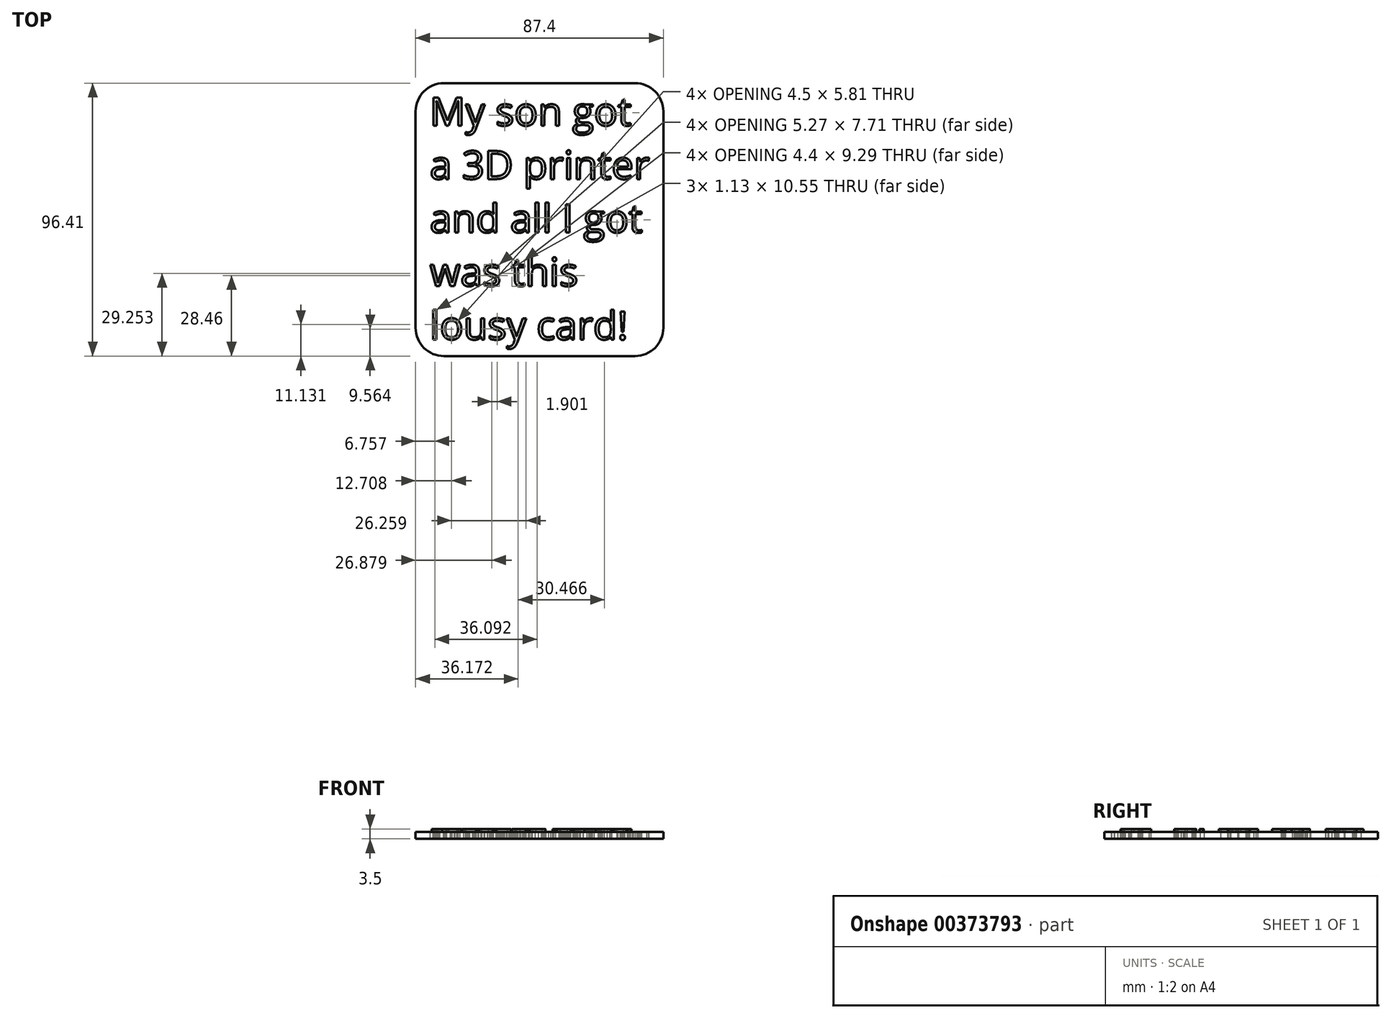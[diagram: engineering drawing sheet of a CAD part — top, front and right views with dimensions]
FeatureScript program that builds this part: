
annotation { "Feature Type Name" : "Feature", "Feature Type Description" : "" }
export const myFeature = defineFeature(function(context is Context, id is Id, definition is map)
    precondition{}
    {
        {
            var Q0;
            Q0=qCreatedBy(makeId("Top.planeOp"),FACE);
            var sketch = newSketch(context, id + "F0", { "sketchPlane" : qUnion([Q0])});
            skText(sketch, "E0", { "text": "My son got  \na 3D printer \nand all I got\nwas this \nlousy card!", "fontName": "OpenSans-Regular.ttf"});
            skLineSegment(sketch, "E1.bottom", {"start": v(0, 0) * mm, "end": v(77.4, 0) * mm, "construction": true});
            skLineSegment(sketch, "E1.top", {"start": v(0, -86.41) * mm, "end": v(77.4, -86.41) * mm, "construction": true});
            skLineSegment(sketch, "E1.left", {"start": v(0, 0) * mm, "end": v(0, -86.41) * mm, "construction": true});
            skLineSegment(sketch, "E1.right", {"start": v(77.4, 0) * mm, "end": v(77.4, -86.41) * mm, "construction": true});
            const initialGuessF0  = {"E0": [0, -0.01, 1, 0, 0.01]};
            skSetInitialGuess(sketch, initialGuessF0);
            skSolve(sketch);
        }
        {
            var Q0;
            Q0=qCreatedBy(makeId("Top.planeOp"),FACE);
            var sketch = newSketch(context, id + "F1", { "sketchPlane" : qUnion([Q0])});
            skLineSegment(sketch, "E2.bottom", {"start": v(-5, 5) * mm, "end": v(82.4, 5) * mm});
            skLineSegment(sketch, "E2.top", {"start": v(-5, -91.41) * mm, "end": v(82.4, -91.41) * mm});
            skLineSegment(sketch, "E2.left", {"start": v(-5, 5) * mm, "end": v(-5, -91.41) * mm});
            skLineSegment(sketch, "E2.right", {"start": v(82.4, 5) * mm, "end": v(82.4, -91.41) * mm});
            skSolve(sketch);
        }
        {
            var Q0;
            Q0=makeQuery(id+"F1.imprint","IMPRINT",FACE,{"disambiguationData":[TD([[makeQuery(id+"F1.imprint","IMPRINT",EDGE,{"derivedFrom":sQuery(id+"F1.wireOp",EDGE,"E2.bottom")}),-1.0]])]});
            extrude(context, id + "F2", {"entities" : qUnion([Q0]), "depth" : 2.5 * mm});
        }
        {
            var Q0;
            Q0 = qSketchRegion(id + "F0", true);
            extrude(context, id + "F3", {"entities" : qUnion([Q0]), "operationType" : NewBodyOperationType.ADD, "depth" : 3.5 * mm});
        }
        {
            var Q0;
            Q0=makeQuery(id+"F3.opExtrude","CAP_FACE",FACE,{"disambiguationData":[OSD([sQuery(id+"F0.wireOp",EDGE,"E0.sketch_text.stroke-18"),sQuery(id+"F0.wireOp",EDGE,"E0.sketch_text.stroke-19"),sQuery(id+"F0.wireOp",EDGE,"E0.sketch_text.stroke-20"),sQuery(id+"F0.wireOp",EDGE,"E0.sketch_text.stroke-21"),sQuery(id+"F0.wireOp",EDGE,"E0.sketch_text.stroke-22"),sQuery(id+"F0.wireOp",EDGE,"E0.sketch_text.stroke-23"),sQuery(id+"F0.wireOp",EDGE,"E0.sketch_text.stroke-24"),sQuery(id+"F0.wireOp",EDGE,"E0.sketch_text.stroke-25"),sQuery(id+"F0.wireOp",EDGE,"E0.sketch_text.stroke-26"),sQuery(id+"F0.wireOp",EDGE,"E0.sketch_text.stroke-27"),sQuery(id+"F0.wireOp",EDGE,"E0.sketch_text.stroke-28"),sQuery(id+"F0.wireOp",EDGE,"E0.sketch_text.stroke-29"),sQuery(id+"F0.wireOp",EDGE,"E0.sketch_text.stroke-30"),sQuery(id+"F0.wireOp",EDGE,"E0.sketch_text.stroke-31"),sQuery(id+"F0.wireOp",EDGE,"E0.sketch_text.stroke-32"),sQuery(id+"F0.wireOp",EDGE,"E0.sketch_text.stroke-33")])],"isStart":false});
            var Q1;
            Q1=makeQuery(id+"F3.opExtrude","CAP_FACE",FACE,{"disambiguationData":[OSD([sQuery(id+"F0.wireOp",EDGE,"E0.sketch_text.stroke-34"),sQuery(id+"F0.wireOp",EDGE,"E0.sketch_text.stroke-35"),sQuery(id+"F0.wireOp",EDGE,"E0.sketch_text.stroke-36"),sQuery(id+"F0.wireOp",EDGE,"E0.sketch_text.stroke-37"),sQuery(id+"F0.wireOp",EDGE,"E0.sketch_text.stroke-38"),sQuery(id+"F0.wireOp",EDGE,"E0.sketch_text.stroke-39"),sQuery(id+"F0.wireOp",EDGE,"E0.sketch_text.stroke-40"),sQuery(id+"F0.wireOp",EDGE,"E0.sketch_text.stroke-41"),sQuery(id+"F0.wireOp",EDGE,"E0.sketch_text.stroke-42"),sQuery(id+"F0.wireOp",EDGE,"E0.sketch_text.stroke-43"),sQuery(id+"F0.wireOp",EDGE,"E0.sketch_text.stroke-44"),sQuery(id+"F0.wireOp",EDGE,"E0.sketch_text.stroke-45"),sQuery(id+"F0.wireOp",EDGE,"E0.sketch_text.stroke-46"),sQuery(id+"F0.wireOp",EDGE,"E0.sketch_text.stroke-47"),sQuery(id+"F0.wireOp",EDGE,"E0.sketch_text.stroke-48"),sQuery(id+"F0.wireOp",EDGE,"E0.sketch_text.stroke-49"),sQuery(id+"F0.wireOp",EDGE,"E0.sketch_text.stroke-50"),sQuery(id+"F0.wireOp",EDGE,"E0.sketch_text.stroke-51"),sQuery(id+"F0.wireOp",EDGE,"E0.sketch_text.stroke-52"),sQuery(id+"F0.wireOp",EDGE,"E0.sketch_text.stroke-53"),sQuery(id+"F0.wireOp",EDGE,"E0.sketch_text.stroke-54"),sQuery(id+"F0.wireOp",EDGE,"E0.sketch_text.stroke-55"),sQuery(id+"F0.wireOp",EDGE,"E0.sketch_text.stroke-56"),sQuery(id+"F0.wireOp",EDGE,"E0.sketch_text.stroke-57"),sQuery(id+"F0.wireOp",EDGE,"E0.sketch_text.stroke-58")])],"isStart":false});
            var Q2;
            Q2=makeQuery(id+"F3.boolean.opBoolean","SPLIT",FACE,{"disambiguationData":[TD([makeQuery(id+"F3.opExtrude","SWEPT_FACE",FACE,{"disambiguationData":[OSD([sQuery(id+"F0.wireOp",EDGE,"E0.sketch_text.stroke-68")])]})])],"derivedFrom":makeQuery(id+"F2.opExtrude","CAP_FACE",FACE,{"disambiguationData":[OSD([sQuery(id+"F1.wireOp",EDGE,"E2.bottom"),sQuery(id+"F1.wireOp",EDGE,"E2.top"),sQuery(id+"F1.wireOp",EDGE,"E2.left"),sQuery(id+"F1.wireOp",EDGE,"E2.right")])],"isStart":false})});
            var Q3;
            Q3=makeQuery(id+"F3.opExtrude","CAP_FACE",FACE,{"disambiguationData":[OSD([sQuery(id+"F0.wireOp",EDGE,"E0.sketch_text.stroke-76"),sQuery(id+"F0.wireOp",EDGE,"E0.sketch_text.stroke-77"),sQuery(id+"F0.wireOp",EDGE,"E0.sketch_text.stroke-78"),sQuery(id+"F0.wireOp",EDGE,"E0.sketch_text.stroke-79"),sQuery(id+"F0.wireOp",EDGE,"E0.sketch_text.stroke-80"),sQuery(id+"F0.wireOp",EDGE,"E0.sketch_text.stroke-81"),sQuery(id+"F0.wireOp",EDGE,"E0.sketch_text.stroke-82"),sQuery(id+"F0.wireOp",EDGE,"E0.sketch_text.stroke-83"),sQuery(id+"F0.wireOp",EDGE,"E0.sketch_text.stroke-84"),sQuery(id+"F0.wireOp",EDGE,"E0.sketch_text.stroke-85"),sQuery(id+"F0.wireOp",EDGE,"E0.sketch_text.stroke-86"),sQuery(id+"F0.wireOp",EDGE,"E0.sketch_text.stroke-87"),sQuery(id+"F0.wireOp",EDGE,"E0.sketch_text.stroke-88"),sQuery(id+"F0.wireOp",EDGE,"E0.sketch_text.stroke-89"),sQuery(id+"F0.wireOp",EDGE,"E0.sketch_text.stroke-90"),sQuery(id+"F0.wireOp",EDGE,"E0.sketch_text.stroke-91"),sQuery(id+"F0.wireOp",EDGE,"E0.sketch_text.stroke-92")])],"isStart":false});
            var Q4;
            Q4=makeQuery(id+"F3.opExtrude","CAP_FACE",FACE,{"disambiguationData":[OSD([sQuery(id+"F0.wireOp",EDGE,"E0.sketch_text.stroke-154"),sQuery(id+"F0.wireOp",EDGE,"E0.sketch_text.stroke-155"),sQuery(id+"F0.wireOp",EDGE,"E0.sketch_text.stroke-156"),sQuery(id+"F0.wireOp",EDGE,"E0.sketch_text.stroke-157"),sQuery(id+"F0.wireOp",EDGE,"E0.sketch_text.stroke-158"),sQuery(id+"F0.wireOp",EDGE,"E0.sketch_text.stroke-159"),sQuery(id+"F0.wireOp",EDGE,"E0.sketch_text.stroke-160"),sQuery(id+"F0.wireOp",EDGE,"E0.sketch_text.stroke-161"),sQuery(id+"F0.wireOp",EDGE,"E0.sketch_text.stroke-162"),sQuery(id+"F0.wireOp",EDGE,"E0.sketch_text.stroke-163"),sQuery(id+"F0.wireOp",EDGE,"E0.sketch_text.stroke-164"),sQuery(id+"F0.wireOp",EDGE,"E0.sketch_text.stroke-165"),sQuery(id+"F0.wireOp",EDGE,"E0.sketch_text.stroke-166"),sQuery(id+"F0.wireOp",EDGE,"E0.sketch_text.stroke-167"),sQuery(id+"F0.wireOp",EDGE,"E0.sketch_text.stroke-168"),sQuery(id+"F0.wireOp",EDGE,"E0.sketch_text.stroke-169"),sQuery(id+"F0.wireOp",EDGE,"E0.sketch_text.stroke-170"),sQuery(id+"F0.wireOp",EDGE,"E0.sketch_text.stroke-171"),sQuery(id+"F0.wireOp",EDGE,"E0.sketch_text.stroke-172")])],"isStart":false});
            var Q5;
            Q5=makeQuery(id+"F3.opExtrude","CAP_FACE",FACE,{"disambiguationData":[OSD([sQuery(id+"F0.wireOp",EDGE,"E0.sketch_text.stroke-200"),sQuery(id+"F0.wireOp",EDGE,"E0.sketch_text.stroke-201"),sQuery(id+"F0.wireOp",EDGE,"E0.sketch_text.stroke-202"),sQuery(id+"F0.wireOp",EDGE,"E0.sketch_text.stroke-203"),sQuery(id+"F0.wireOp",EDGE,"E0.sketch_text.stroke-204"),sQuery(id+"F0.wireOp",EDGE,"E0.sketch_text.stroke-205"),sQuery(id+"F0.wireOp",EDGE,"E0.sketch_text.stroke-206"),sQuery(id+"F0.wireOp",EDGE,"E0.sketch_text.stroke-207"),sQuery(id+"F0.wireOp",EDGE,"E0.sketch_text.stroke-208"),sQuery(id+"F0.wireOp",EDGE,"E0.sketch_text.stroke-209"),sQuery(id+"F0.wireOp",EDGE,"E0.sketch_text.stroke-210"),sQuery(id+"F0.wireOp",EDGE,"E0.sketch_text.stroke-211"),sQuery(id+"F0.wireOp",EDGE,"E0.sketch_text.stroke-212"),sQuery(id+"F0.wireOp",EDGE,"E0.sketch_text.stroke-213"),sQuery(id+"F0.wireOp",EDGE,"E0.sketch_text.stroke-214"),sQuery(id+"F0.wireOp",EDGE,"E0.sketch_text.stroke-215"),sQuery(id+"F0.wireOp",EDGE,"E0.sketch_text.stroke-216"),sQuery(id+"F0.wireOp",EDGE,"E0.sketch_text.stroke-217"),sQuery(id+"F0.wireOp",EDGE,"E0.sketch_text.stroke-218"),sQuery(id+"F0.wireOp",EDGE,"E0.sketch_text.stroke-219"),sQuery(id+"F0.wireOp",EDGE,"E0.sketch_text.stroke-220"),sQuery(id+"F0.wireOp",EDGE,"E0.sketch_text.stroke-221"),sQuery(id+"F0.wireOp",EDGE,"E0.sketch_text.stroke-222"),sQuery(id+"F0.wireOp",EDGE,"E0.sketch_text.stroke-223"),sQuery(id+"F0.wireOp",EDGE,"E0.sketch_text.stroke-224"),sQuery(id+"F0.wireOp",EDGE,"E0.sketch_text.stroke-225"),sQuery(id+"F0.wireOp",EDGE,"E0.sketch_text.stroke-226"),sQuery(id+"F0.wireOp",EDGE,"E0.sketch_text.stroke-227")])],"isStart":false});
            var Q6;
            Q6=makeQuery(id+"F3.opExtrude","CAP_FACE",FACE,{"disambiguationData":[OSD([sQuery(id+"F0.wireOp",EDGE,"E0.sketch_text.stroke-267"),sQuery(id+"F0.wireOp",EDGE,"E0.sketch_text.stroke-268"),sQuery(id+"F0.wireOp",EDGE,"E0.sketch_text.stroke-269"),sQuery(id+"F0.wireOp",EDGE,"E0.sketch_text.stroke-270"),sQuery(id+"F0.wireOp",EDGE,"E0.sketch_text.stroke-271"),sQuery(id+"F0.wireOp",EDGE,"E0.sketch_text.stroke-272"),sQuery(id+"F0.wireOp",EDGE,"E0.sketch_text.stroke-273"),sQuery(id+"F0.wireOp",EDGE,"E0.sketch_text.stroke-274"),sQuery(id+"F0.wireOp",EDGE,"E0.sketch_text.stroke-275"),sQuery(id+"F0.wireOp",EDGE,"E0.sketch_text.stroke-276"),sQuery(id+"F0.wireOp",EDGE,"E0.sketch_text.stroke-277"),sQuery(id+"F0.wireOp",EDGE,"E0.sketch_text.stroke-278"),sQuery(id+"F0.wireOp",EDGE,"E0.sketch_text.stroke-279")])],"isStart":false});
            var Q7;
            Q7=makeQuery(id+"F3.opExtrude","CAP_FACE",FACE,{"disambiguationData":[OSD([sQuery(id+"F0.wireOp",EDGE,"E0.sketch_text.stroke-284"),sQuery(id+"F0.wireOp",EDGE,"E0.sketch_text.stroke-285"),sQuery(id+"F0.wireOp",EDGE,"E0.sketch_text.stroke-286"),sQuery(id+"F0.wireOp",EDGE,"E0.sketch_text.stroke-287"),sQuery(id+"F0.wireOp",EDGE,"E0.sketch_text.stroke-288"),sQuery(id+"F0.wireOp",EDGE,"E0.sketch_text.stroke-289"),sQuery(id+"F0.wireOp",EDGE,"E0.sketch_text.stroke-290"),sQuery(id+"F0.wireOp",EDGE,"E0.sketch_text.stroke-291")])],"isStart":false});
            var Q8;
            Q8=makeQuery(id+"F3.opExtrude","CAP_FACE",FACE,{"disambiguationData":[OSD([sQuery(id+"F0.wireOp",EDGE,"E0.sketch_text.stroke-292"),sQuery(id+"F0.wireOp",EDGE,"E0.sketch_text.stroke-293"),sQuery(id+"F0.wireOp",EDGE,"E0.sketch_text.stroke-294"),sQuery(id+"F0.wireOp",EDGE,"E0.sketch_text.stroke-295"),sQuery(id+"F0.wireOp",EDGE,"E0.sketch_text.stroke-296"),sQuery(id+"F0.wireOp",EDGE,"E0.sketch_text.stroke-297"),sQuery(id+"F0.wireOp",EDGE,"E0.sketch_text.stroke-298"),sQuery(id+"F0.wireOp",EDGE,"E0.sketch_text.stroke-299"),sQuery(id+"F0.wireOp",EDGE,"E0.sketch_text.stroke-300"),sQuery(id+"F0.wireOp",EDGE,"E0.sketch_text.stroke-301"),sQuery(id+"F0.wireOp",EDGE,"E0.sketch_text.stroke-302"),sQuery(id+"F0.wireOp",EDGE,"E0.sketch_text.stroke-303"),sQuery(id+"F0.wireOp",EDGE,"E0.sketch_text.stroke-304"),sQuery(id+"F0.wireOp",EDGE,"E0.sketch_text.stroke-305"),sQuery(id+"F0.wireOp",EDGE,"E0.sketch_text.stroke-306"),sQuery(id+"F0.wireOp",EDGE,"E0.sketch_text.stroke-307"),sQuery(id+"F0.wireOp",EDGE,"E0.sketch_text.stroke-308")])],"isStart":false});
            var Q9;
            Q9=makeQuery(id+"F3.boolean.opBoolean","SPLIT",FACE,{"disambiguationData":[TD([makeQuery(id+"F3.opExtrude","SWEPT_FACE",FACE,{"disambiguationData":[OSD([sQuery(id+"F0.wireOp",EDGE,"E0.sketch_text.stroke-146")])]})])],"derivedFrom":makeQuery(id+"F2.opExtrude","CAP_FACE",FACE,{"disambiguationData":[OSD([sQuery(id+"F1.wireOp",EDGE,"E2.bottom"),sQuery(id+"F1.wireOp",EDGE,"E2.top"),sQuery(id+"F1.wireOp",EDGE,"E2.left"),sQuery(id+"F1.wireOp",EDGE,"E2.right")])],"isStart":false})});
            var Q10;
            Q10=makeQuery(id+"F3.boolean.opBoolean","SPLIT",FACE,{"disambiguationData":[TD([makeQuery(id+"F3.opExtrude","SWEPT_FACE",FACE,{"disambiguationData":[OSD([sQuery(id+"F0.wireOp",EDGE,"E0.sketch_text.stroke-131")])]})])],"derivedFrom":makeQuery(id+"F2.opExtrude","CAP_FACE",FACE,{"disambiguationData":[OSD([sQuery(id+"F1.wireOp",EDGE,"E2.bottom"),sQuery(id+"F1.wireOp",EDGE,"E2.top"),sQuery(id+"F1.wireOp",EDGE,"E2.left"),sQuery(id+"F1.wireOp",EDGE,"E2.right")])],"isStart":false})});
            var Q11;
            Q11=makeQuery(id+"F3.boolean.opBoolean","SPLIT",FACE,{"disambiguationData":[TD([makeQuery(id+"F3.opExtrude","SWEPT_FACE",FACE,{"disambiguationData":[OSD([sQuery(id+"F0.wireOp",EDGE,"E0.sketch_text.stroke-122")])]})])],"derivedFrom":makeQuery(id+"F2.opExtrude","CAP_FACE",FACE,{"disambiguationData":[OSD([sQuery(id+"F1.wireOp",EDGE,"E2.bottom"),sQuery(id+"F1.wireOp",EDGE,"E2.top"),sQuery(id+"F1.wireOp",EDGE,"E2.left"),sQuery(id+"F1.wireOp",EDGE,"E2.right")])],"isStart":false})});
            var Q12;
            Q12=makeQuery(id+"F3.boolean.opBoolean","SPLIT",FACE,{"disambiguationData":[TD([makeQuery(id+"F3.opExtrude","SWEPT_FACE",FACE,{"disambiguationData":[OSD([sQuery(id+"F0.wireOp",EDGE,"E0.sketch_text.stroke-235")])]})])],"derivedFrom":makeQuery(id+"F2.opExtrude","CAP_FACE",FACE,{"disambiguationData":[OSD([sQuery(id+"F1.wireOp",EDGE,"E2.bottom"),sQuery(id+"F1.wireOp",EDGE,"E2.top"),sQuery(id+"F1.wireOp",EDGE,"E2.left"),sQuery(id+"F1.wireOp",EDGE,"E2.right")])],"isStart":false})});
            var Q13;
            Q13=makeQuery(id+"F3.boolean.opBoolean","SPLIT",FACE,{"disambiguationData":[TD([makeQuery(id+"F3.opExtrude","SWEPT_FACE",FACE,{"disambiguationData":[OSD([sQuery(id+"F0.wireOp",EDGE,"E0.sketch_text.stroke-192")])]})])],"derivedFrom":makeQuery(id+"F2.opExtrude","CAP_FACE",FACE,{"disambiguationData":[OSD([sQuery(id+"F1.wireOp",EDGE,"E2.bottom"),sQuery(id+"F1.wireOp",EDGE,"E2.top"),sQuery(id+"F1.wireOp",EDGE,"E2.left"),sQuery(id+"F1.wireOp",EDGE,"E2.right")])],"isStart":false})});
            var Q14;
            Q14=makeQuery(id+"F3.opExtrude","CAP_FACE",FACE,{"disambiguationData":[OSD([sQuery(id+"F0.wireOp",EDGE,"E0.sketch_text.stroke-309"),sQuery(id+"F0.wireOp",EDGE,"E0.sketch_text.stroke-310"),sQuery(id+"F0.wireOp",EDGE,"E0.sketch_text.stroke-311"),sQuery(id+"F0.wireOp",EDGE,"E0.sketch_text.stroke-312"),sQuery(id+"F0.wireOp",EDGE,"E0.sketch_text.stroke-313"),sQuery(id+"F0.wireOp",EDGE,"E0.sketch_text.stroke-314"),sQuery(id+"F0.wireOp",EDGE,"E0.sketch_text.stroke-315"),sQuery(id+"F0.wireOp",EDGE,"E0.sketch_text.stroke-316"),sQuery(id+"F0.wireOp",EDGE,"E0.sketch_text.stroke-317"),sQuery(id+"F0.wireOp",EDGE,"E0.sketch_text.stroke-318"),sQuery(id+"F0.wireOp",EDGE,"E0.sketch_text.stroke-319"),sQuery(id+"F0.wireOp",EDGE,"E0.sketch_text.stroke-320"),sQuery(id+"F0.wireOp",EDGE,"E0.sketch_text.stroke-321"),sQuery(id+"F0.wireOp",EDGE,"E0.sketch_text.stroke-322"),sQuery(id+"F0.wireOp",EDGE,"E0.sketch_text.stroke-323"),sQuery(id+"F0.wireOp",EDGE,"E0.sketch_text.stroke-324"),sQuery(id+"F0.wireOp",EDGE,"E0.sketch_text.stroke-325"),sQuery(id+"F0.wireOp",EDGE,"E0.sketch_text.stroke-326"),sQuery(id+"F0.wireOp",EDGE,"E0.sketch_text.stroke-327")])],"isStart":false});
            var Q15;
            Q15=makeQuery(id+"F3.boolean.opBoolean","SPLIT",FACE,{"disambiguationData":[TD([makeQuery(id+"F3.opExtrude","SWEPT_FACE",FACE,{"disambiguationData":[OSD([sQuery(id+"F0.wireOp",EDGE,"E0.sketch_text.stroke-342")])]})])],"derivedFrom":makeQuery(id+"F2.opExtrude","CAP_FACE",FACE,{"disambiguationData":[OSD([sQuery(id+"F1.wireOp",EDGE,"E2.bottom"),sQuery(id+"F1.wireOp",EDGE,"E2.top"),sQuery(id+"F1.wireOp",EDGE,"E2.left"),sQuery(id+"F1.wireOp",EDGE,"E2.right")])],"isStart":false})});
            var Q16;
            Q16=makeQuery(id+"F3.opExtrude","CAP_FACE",FACE,{"disambiguationData":[OSD([sQuery(id+"F0.wireOp",EDGE,"E0.sketch_text.stroke-347"),sQuery(id+"F0.wireOp",EDGE,"E0.sketch_text.stroke-348"),sQuery(id+"F0.wireOp",EDGE,"E0.sketch_text.stroke-349"),sQuery(id+"F0.wireOp",EDGE,"E0.sketch_text.stroke-350"),sQuery(id+"F0.wireOp",EDGE,"E0.sketch_text.stroke-351"),sQuery(id+"F0.wireOp",EDGE,"E0.sketch_text.stroke-352"),sQuery(id+"F0.wireOp",EDGE,"E0.sketch_text.stroke-353"),sQuery(id+"F0.wireOp",EDGE,"E0.sketch_text.stroke-354"),sQuery(id+"F0.wireOp",EDGE,"E0.sketch_text.stroke-355"),sQuery(id+"F0.wireOp",EDGE,"E0.sketch_text.stroke-356"),sQuery(id+"F0.wireOp",EDGE,"E0.sketch_text.stroke-357"),sQuery(id+"F0.wireOp",EDGE,"E0.sketch_text.stroke-358"),sQuery(id+"F0.wireOp",EDGE,"E0.sketch_text.stroke-359")])],"isStart":false});
            var Q17;
            Q17=makeQuery(id+"F3.boolean.opBoolean","SPLIT",FACE,{"disambiguationData":[TD([makeQuery(id+"F3.opExtrude","SWEPT_FACE",FACE,{"disambiguationData":[OSD([sQuery(id+"F0.wireOp",EDGE,"E0.sketch_text.stroke-379")])]})])],"derivedFrom":makeQuery(id+"F2.opExtrude","CAP_FACE",FACE,{"disambiguationData":[OSD([sQuery(id+"F1.wireOp",EDGE,"E2.bottom"),sQuery(id+"F1.wireOp",EDGE,"E2.top"),sQuery(id+"F1.wireOp",EDGE,"E2.left"),sQuery(id+"F1.wireOp",EDGE,"E2.right")])],"isStart":false})});
            var Q18;
            Q18=makeQuery(id+"F3.opExtrude","CAP_FACE",FACE,{"disambiguationData":[OSD([sQuery(id+"F0.wireOp",EDGE,"E0.sketch_text.stroke-387"),sQuery(id+"F0.wireOp",EDGE,"E0.sketch_text.stroke-388"),sQuery(id+"F0.wireOp",EDGE,"E0.sketch_text.stroke-389"),sQuery(id+"F0.wireOp",EDGE,"E0.sketch_text.stroke-390"),sQuery(id+"F0.wireOp",EDGE,"E0.sketch_text.stroke-391"),sQuery(id+"F0.wireOp",EDGE,"E0.sketch_text.stroke-392"),sQuery(id+"F0.wireOp",EDGE,"E0.sketch_text.stroke-393"),sQuery(id+"F0.wireOp",EDGE,"E0.sketch_text.stroke-394"),sQuery(id+"F0.wireOp",EDGE,"E0.sketch_text.stroke-395"),sQuery(id+"F0.wireOp",EDGE,"E0.sketch_text.stroke-396"),sQuery(id+"F0.wireOp",EDGE,"E0.sketch_text.stroke-397"),sQuery(id+"F0.wireOp",EDGE,"E0.sketch_text.stroke-398"),sQuery(id+"F0.wireOp",EDGE,"E0.sketch_text.stroke-399"),sQuery(id+"F0.wireOp",EDGE,"E0.sketch_text.stroke-400"),sQuery(id+"F0.wireOp",EDGE,"E0.sketch_text.stroke-401"),sQuery(id+"F0.wireOp",EDGE,"E0.sketch_text.stroke-402"),sQuery(id+"F0.wireOp",EDGE,"E0.sketch_text.stroke-403")])],"isStart":false});
            var Q19;
            Q19=makeQuery(id+"F3.boolean.opBoolean","SPLIT",FACE,{"disambiguationData":[TD([makeQuery(id+"F3.opExtrude","SWEPT_FACE",FACE,{"disambiguationData":[OSD([sQuery(id+"F0.wireOp",EDGE,"E0.sketch_text.stroke-419")])]})])],"derivedFrom":makeQuery(id+"F2.opExtrude","CAP_FACE",FACE,{"disambiguationData":[OSD([sQuery(id+"F1.wireOp",EDGE,"E2.bottom"),sQuery(id+"F1.wireOp",EDGE,"E2.top"),sQuery(id+"F1.wireOp",EDGE,"E2.left"),sQuery(id+"F1.wireOp",EDGE,"E2.right")])],"isStart":false})});
            var Q20;
            Q20=makeQuery(id+"F3.boolean.opBoolean","SPLIT",FACE,{"disambiguationData":[TD([makeQuery(id+"F3.opExtrude","SWEPT_FACE",FACE,{"disambiguationData":[OSD([sQuery(id+"F0.wireOp",EDGE,"E0.sketch_text.stroke-447")])]})])],"derivedFrom":makeQuery(id+"F2.opExtrude","CAP_FACE",FACE,{"disambiguationData":[OSD([sQuery(id+"F1.wireOp",EDGE,"E2.bottom"),sQuery(id+"F1.wireOp",EDGE,"E2.top"),sQuery(id+"F1.wireOp",EDGE,"E2.left"),sQuery(id+"F1.wireOp",EDGE,"E2.right")])],"isStart":false})});
            var Q21;
            Q21=makeQuery(id+"F3.opExtrude","CAP_FACE",FACE,{"disambiguationData":[OSD([sQuery(id+"F0.wireOp",EDGE,"E0.sketch_text.stroke-455"),sQuery(id+"F0.wireOp",EDGE,"E0.sketch_text.stroke-456"),sQuery(id+"F0.wireOp",EDGE,"E0.sketch_text.stroke-457"),sQuery(id+"F0.wireOp",EDGE,"E0.sketch_text.stroke-458")])],"isStart":false});
            var Q22;
            Q22=makeQuery(id+"F3.opExtrude","CAP_FACE",FACE,{"disambiguationData":[OSD([sQuery(id+"F0.wireOp",EDGE,"E0.sketch_text.stroke-459"),sQuery(id+"F0.wireOp",EDGE,"E0.sketch_text.stroke-460"),sQuery(id+"F0.wireOp",EDGE,"E0.sketch_text.stroke-461"),sQuery(id+"F0.wireOp",EDGE,"E0.sketch_text.stroke-462")])],"isStart":false});
            var Q23;
            Q23=makeQuery(id+"F3.opExtrude","CAP_FACE",FACE,{"disambiguationData":[OSD([sQuery(id+"F0.wireOp",EDGE,"E0.sketch_text.stroke-463"),sQuery(id+"F0.wireOp",EDGE,"E0.sketch_text.stroke-464"),sQuery(id+"F0.wireOp",EDGE,"E0.sketch_text.stroke-465"),sQuery(id+"F0.wireOp",EDGE,"E0.sketch_text.stroke-466")])],"isStart":false});
            var Q24;
            Q24=makeQuery(id+"F3.boolean.opBoolean","SPLIT",FACE,{"disambiguationData":[TD([makeQuery(id+"F3.opExtrude","SWEPT_FACE",FACE,{"disambiguationData":[OSD([sQuery(id+"F0.wireOp",EDGE,"E0.sketch_text.stroke-505")])]})])],"derivedFrom":makeQuery(id+"F2.opExtrude","CAP_FACE",FACE,{"disambiguationData":[OSD([sQuery(id+"F1.wireOp",EDGE,"E2.bottom"),sQuery(id+"F1.wireOp",EDGE,"E2.top"),sQuery(id+"F1.wireOp",EDGE,"E2.left"),sQuery(id+"F1.wireOp",EDGE,"E2.right")])],"isStart":false})});
            var Q25;
            Q25=makeQuery(id+"F3.boolean.opBoolean","SPLIT",FACE,{"disambiguationData":[TD([makeQuery(id+"F3.opExtrude","SWEPT_FACE",FACE,{"disambiguationData":[OSD([sQuery(id+"F0.wireOp",EDGE,"E0.sketch_text.stroke-496")])]})])],"derivedFrom":makeQuery(id+"F2.opExtrude","CAP_FACE",FACE,{"disambiguationData":[OSD([sQuery(id+"F1.wireOp",EDGE,"E2.bottom"),sQuery(id+"F1.wireOp",EDGE,"E2.top"),sQuery(id+"F1.wireOp",EDGE,"E2.left"),sQuery(id+"F1.wireOp",EDGE,"E2.right")])],"isStart":false})});
            var Q26;
            Q26=makeQuery(id+"F3.boolean.opBoolean","SPLIT",FACE,{"disambiguationData":[TD([makeQuery(id+"F3.opExtrude","SWEPT_FACE",FACE,{"disambiguationData":[OSD([sQuery(id+"F0.wireOp",EDGE,"E0.sketch_text.stroke-520")])]})])],"derivedFrom":makeQuery(id+"F2.opExtrude","CAP_FACE",FACE,{"disambiguationData":[OSD([sQuery(id+"F1.wireOp",EDGE,"E2.bottom"),sQuery(id+"F1.wireOp",EDGE,"E2.top"),sQuery(id+"F1.wireOp",EDGE,"E2.left"),sQuery(id+"F1.wireOp",EDGE,"E2.right")])],"isStart":false})});
            var Q27;
            Q27=makeQuery(id+"F3.opExtrude","CAP_FACE",FACE,{"disambiguationData":[OSD([sQuery(id+"F0.wireOp",EDGE,"E0.sketch_text.stroke-528"),sQuery(id+"F0.wireOp",EDGE,"E0.sketch_text.stroke-529"),sQuery(id+"F0.wireOp",EDGE,"E0.sketch_text.stroke-530"),sQuery(id+"F0.wireOp",EDGE,"E0.sketch_text.stroke-531"),sQuery(id+"F0.wireOp",EDGE,"E0.sketch_text.stroke-532"),sQuery(id+"F0.wireOp",EDGE,"E0.sketch_text.stroke-533"),sQuery(id+"F0.wireOp",EDGE,"E0.sketch_text.stroke-534"),sQuery(id+"F0.wireOp",EDGE,"E0.sketch_text.stroke-535"),sQuery(id+"F0.wireOp",EDGE,"E0.sketch_text.stroke-536"),sQuery(id+"F0.wireOp",EDGE,"E0.sketch_text.stroke-537"),sQuery(id+"F0.wireOp",EDGE,"E0.sketch_text.stroke-538"),sQuery(id+"F0.wireOp",EDGE,"E0.sketch_text.stroke-539"),sQuery(id+"F0.wireOp",EDGE,"E0.sketch_text.stroke-540"),sQuery(id+"F0.wireOp",EDGE,"E0.sketch_text.stroke-541"),sQuery(id+"F0.wireOp",EDGE,"E0.sketch_text.stroke-542"),sQuery(id+"F0.wireOp",EDGE,"E0.sketch_text.stroke-543"),sQuery(id+"F0.wireOp",EDGE,"E0.sketch_text.stroke-544"),sQuery(id+"F0.wireOp",EDGE,"E0.sketch_text.stroke-545"),sQuery(id+"F0.wireOp",EDGE,"E0.sketch_text.stroke-546")])],"isStart":false});
            var Q28;
            Q28=makeQuery(id+"F3.opExtrude","CAP_FACE",FACE,{"disambiguationData":[OSD([sQuery(id+"F0.wireOp",EDGE,"E0.sketch_text.stroke-547"),sQuery(id+"F0.wireOp",EDGE,"E0.sketch_text.stroke-548"),sQuery(id+"F0.wireOp",EDGE,"E0.sketch_text.stroke-549"),sQuery(id+"F0.wireOp",EDGE,"E0.sketch_text.stroke-550"),sQuery(id+"F0.wireOp",EDGE,"E0.sketch_text.stroke-551"),sQuery(id+"F0.wireOp",EDGE,"E0.sketch_text.stroke-552"),sQuery(id+"F0.wireOp",EDGE,"E0.sketch_text.stroke-553"),sQuery(id+"F0.wireOp",EDGE,"E0.sketch_text.stroke-554"),sQuery(id+"F0.wireOp",EDGE,"E0.sketch_text.stroke-555"),sQuery(id+"F0.wireOp",EDGE,"E0.sketch_text.stroke-556"),sQuery(id+"F0.wireOp",EDGE,"E0.sketch_text.stroke-557"),sQuery(id+"F0.wireOp",EDGE,"E0.sketch_text.stroke-558"),sQuery(id+"F0.wireOp",EDGE,"E0.sketch_text.stroke-559"),sQuery(id+"F0.wireOp",EDGE,"E0.sketch_text.stroke-560"),sQuery(id+"F0.wireOp",EDGE,"E0.sketch_text.stroke-561"),sQuery(id+"F0.wireOp",EDGE,"E0.sketch_text.stroke-562"),sQuery(id+"F0.wireOp",EDGE,"E0.sketch_text.stroke-563"),sQuery(id+"F0.wireOp",EDGE,"E0.sketch_text.stroke-564"),sQuery(id+"F0.wireOp",EDGE,"E0.sketch_text.stroke-565"),sQuery(id+"F0.wireOp",EDGE,"E0.sketch_text.stroke-566"),sQuery(id+"F0.wireOp",EDGE,"E0.sketch_text.stroke-567"),sQuery(id+"F0.wireOp",EDGE,"E0.sketch_text.stroke-568"),sQuery(id+"F0.wireOp",EDGE,"E0.sketch_text.stroke-569")])],"isStart":false});
            var Q29;
            Q29=makeQuery(id+"F3.boolean.opBoolean","SPLIT",FACE,{"disambiguationData":[TD([makeQuery(id+"F3.opExtrude","SWEPT_FACE",FACE,{"disambiguationData":[OSD([sQuery(id+"F0.wireOp",EDGE,"E0.sketch_text.stroke-589")])]})])],"derivedFrom":makeQuery(id+"F2.opExtrude","CAP_FACE",FACE,{"disambiguationData":[OSD([sQuery(id+"F1.wireOp",EDGE,"E2.bottom"),sQuery(id+"F1.wireOp",EDGE,"E2.top"),sQuery(id+"F1.wireOp",EDGE,"E2.left"),sQuery(id+"F1.wireOp",EDGE,"E2.right")])],"isStart":false})});
            var Q30;
            Q30=makeQuery(id+"F3.opExtrude","CAP_FACE",FACE,{"disambiguationData":[OSD([sQuery(id+"F0.wireOp",EDGE,"E0.sketch_text.stroke-597"),sQuery(id+"F0.wireOp",EDGE,"E0.sketch_text.stroke-598"),sQuery(id+"F0.wireOp",EDGE,"E0.sketch_text.stroke-599"),sQuery(id+"F0.wireOp",EDGE,"E0.sketch_text.stroke-600"),sQuery(id+"F0.wireOp",EDGE,"E0.sketch_text.stroke-601"),sQuery(id+"F0.wireOp",EDGE,"E0.sketch_text.stroke-602"),sQuery(id+"F0.wireOp",EDGE,"E0.sketch_text.stroke-603"),sQuery(id+"F0.wireOp",EDGE,"E0.sketch_text.stroke-604"),sQuery(id+"F0.wireOp",EDGE,"E0.sketch_text.stroke-605"),sQuery(id+"F0.wireOp",EDGE,"E0.sketch_text.stroke-606"),sQuery(id+"F0.wireOp",EDGE,"E0.sketch_text.stroke-607"),sQuery(id+"F0.wireOp",EDGE,"E0.sketch_text.stroke-608"),sQuery(id+"F0.wireOp",EDGE,"E0.sketch_text.stroke-609"),sQuery(id+"F0.wireOp",EDGE,"E0.sketch_text.stroke-610"),sQuery(id+"F0.wireOp",EDGE,"E0.sketch_text.stroke-611"),sQuery(id+"F0.wireOp",EDGE,"E0.sketch_text.stroke-612"),sQuery(id+"F0.wireOp",EDGE,"E0.sketch_text.stroke-613"),sQuery(id+"F0.wireOp",EDGE,"E0.sketch_text.stroke-614"),sQuery(id+"F0.wireOp",EDGE,"E0.sketch_text.stroke-615"),sQuery(id+"F0.wireOp",EDGE,"E0.sketch_text.stroke-616"),sQuery(id+"F0.wireOp",EDGE,"E0.sketch_text.stroke-617"),sQuery(id+"F0.wireOp",EDGE,"E0.sketch_text.stroke-618"),sQuery(id+"F0.wireOp",EDGE,"E0.sketch_text.stroke-619"),sQuery(id+"F0.wireOp",EDGE,"E0.sketch_text.stroke-620"),sQuery(id+"F0.wireOp",EDGE,"E0.sketch_text.stroke-621")])],"isStart":false});
            var Q31;
            Q31=makeQuery(id+"F3.opExtrude","CAP_FACE",FACE,{"disambiguationData":[OSD([sQuery(id+"F0.wireOp",EDGE,"E0.sketch_text.stroke-622"),sQuery(id+"F0.wireOp",EDGE,"E0.sketch_text.stroke-623"),sQuery(id+"F0.wireOp",EDGE,"E0.sketch_text.stroke-624"),sQuery(id+"F0.wireOp",EDGE,"E0.sketch_text.stroke-625"),sQuery(id+"F0.wireOp",EDGE,"E0.sketch_text.stroke-626"),sQuery(id+"F0.wireOp",EDGE,"E0.sketch_text.stroke-627"),sQuery(id+"F0.wireOp",EDGE,"E0.sketch_text.stroke-628"),sQuery(id+"F0.wireOp",EDGE,"E0.sketch_text.stroke-629"),sQuery(id+"F0.wireOp",EDGE,"E0.sketch_text.stroke-630"),sQuery(id+"F0.wireOp",EDGE,"E0.sketch_text.stroke-631"),sQuery(id+"F0.wireOp",EDGE,"E0.sketch_text.stroke-632"),sQuery(id+"F0.wireOp",EDGE,"E0.sketch_text.stroke-633"),sQuery(id+"F0.wireOp",EDGE,"E0.sketch_text.stroke-634"),sQuery(id+"F0.wireOp",EDGE,"E0.sketch_text.stroke-635"),sQuery(id+"F0.wireOp",EDGE,"E0.sketch_text.stroke-636"),sQuery(id+"F0.wireOp",EDGE,"E0.sketch_text.stroke-637"),sQuery(id+"F0.wireOp",EDGE,"E0.sketch_text.stroke-638"),sQuery(id+"F0.wireOp",EDGE,"E0.sketch_text.stroke-639"),sQuery(id+"F0.wireOp",EDGE,"E0.sketch_text.stroke-640")])],"isStart":false});
            var Q32;
            Q32=makeQuery(id+"F3.opExtrude","CAP_FACE",FACE,{"disambiguationData":[OSD([sQuery(id+"F0.wireOp",EDGE,"E0.sketch_text.stroke-641"),sQuery(id+"F0.wireOp",EDGE,"E0.sketch_text.stroke-642"),sQuery(id+"F0.wireOp",EDGE,"E0.sketch_text.stroke-643"),sQuery(id+"F0.wireOp",EDGE,"E0.sketch_text.stroke-644"),sQuery(id+"F0.wireOp",EDGE,"E0.sketch_text.stroke-645"),sQuery(id+"F0.wireOp",EDGE,"E0.sketch_text.stroke-646"),sQuery(id+"F0.wireOp",EDGE,"E0.sketch_text.stroke-647"),sQuery(id+"F0.wireOp",EDGE,"E0.sketch_text.stroke-648"),sQuery(id+"F0.wireOp",EDGE,"E0.sketch_text.stroke-649"),sQuery(id+"F0.wireOp",EDGE,"E0.sketch_text.stroke-650"),sQuery(id+"F0.wireOp",EDGE,"E0.sketch_text.stroke-651"),sQuery(id+"F0.wireOp",EDGE,"E0.sketch_text.stroke-652"),sQuery(id+"F0.wireOp",EDGE,"E0.sketch_text.stroke-653"),sQuery(id+"F0.wireOp",EDGE,"E0.sketch_text.stroke-654"),sQuery(id+"F0.wireOp",EDGE,"E0.sketch_text.stroke-655"),sQuery(id+"F0.wireOp",EDGE,"E0.sketch_text.stroke-656"),sQuery(id+"F0.wireOp",EDGE,"E0.sketch_text.stroke-657"),sQuery(id+"F0.wireOp",EDGE,"E0.sketch_text.stroke-658")])],"isStart":false});
            var Q33;
            Q33=makeQuery(id+"F3.opExtrude","CAP_FACE",FACE,{"disambiguationData":[OSD([sQuery(id+"F0.wireOp",EDGE,"E0.sketch_text.stroke-659"),sQuery(id+"F0.wireOp",EDGE,"E0.sketch_text.stroke-660"),sQuery(id+"F0.wireOp",EDGE,"E0.sketch_text.stroke-661"),sQuery(id+"F0.wireOp",EDGE,"E0.sketch_text.stroke-662")])],"isStart":false});
            var Q34;
            Q34=makeQuery(id+"F3.opExtrude","CAP_FACE",FACE,{"disambiguationData":[OSD([sQuery(id+"F0.wireOp",EDGE,"E0.sketch_text.stroke-671"),sQuery(id+"F0.wireOp",EDGE,"E0.sketch_text.stroke-672"),sQuery(id+"F0.wireOp",EDGE,"E0.sketch_text.stroke-673"),sQuery(id+"F0.wireOp",EDGE,"E0.sketch_text.stroke-674"),sQuery(id+"F0.wireOp",EDGE,"E0.sketch_text.stroke-675"),sQuery(id+"F0.wireOp",EDGE,"E0.sketch_text.stroke-676"),sQuery(id+"F0.wireOp",EDGE,"E0.sketch_text.stroke-677"),sQuery(id+"F0.wireOp",EDGE,"E0.sketch_text.stroke-678"),sQuery(id+"F0.wireOp",EDGE,"E0.sketch_text.stroke-679"),sQuery(id+"F0.wireOp",EDGE,"E0.sketch_text.stroke-680"),sQuery(id+"F0.wireOp",EDGE,"E0.sketch_text.stroke-681"),sQuery(id+"F0.wireOp",EDGE,"E0.sketch_text.stroke-682"),sQuery(id+"F0.wireOp",EDGE,"E0.sketch_text.stroke-683"),sQuery(id+"F0.wireOp",EDGE,"E0.sketch_text.stroke-684"),sQuery(id+"F0.wireOp",EDGE,"E0.sketch_text.stroke-685"),sQuery(id+"F0.wireOp",EDGE,"E0.sketch_text.stroke-686"),sQuery(id+"F0.wireOp",EDGE,"E0.sketch_text.stroke-687"),sQuery(id+"F0.wireOp",EDGE,"E0.sketch_text.stroke-688"),sQuery(id+"F0.wireOp",EDGE,"E0.sketch_text.stroke-689"),sQuery(id+"F0.wireOp",EDGE,"E0.sketch_text.stroke-690"),sQuery(id+"F0.wireOp",EDGE,"E0.sketch_text.stroke-691"),sQuery(id+"F0.wireOp",EDGE,"E0.sketch_text.stroke-692"),sQuery(id+"F0.wireOp",EDGE,"E0.sketch_text.stroke-693"),sQuery(id+"F0.wireOp",EDGE,"E0.sketch_text.stroke-694"),sQuery(id+"F0.wireOp",EDGE,"E0.sketch_text.stroke-695")])],"isStart":false});
            var Q35;
            Q35=makeQuery(id+"F3.opExtrude","CAP_FACE",FACE,{"disambiguationData":[OSD([sQuery(id+"F0.wireOp",EDGE,"E0.sketch_text.stroke-696"),sQuery(id+"F0.wireOp",EDGE,"E0.sketch_text.stroke-697"),sQuery(id+"F0.wireOp",EDGE,"E0.sketch_text.stroke-698"),sQuery(id+"F0.wireOp",EDGE,"E0.sketch_text.stroke-699")])],"isStart":false});
            var Q36;
            Q36=makeQuery(id+"F3.boolean.opBoolean","SPLIT",FACE,{"disambiguationData":[TD([makeQuery(id+"F3.opExtrude","SWEPT_FACE",FACE,{"disambiguationData":[OSD([sQuery(id+"F0.wireOp",EDGE,"E0.sketch_text.stroke-709")])]})])],"derivedFrom":makeQuery(id+"F2.opExtrude","CAP_FACE",FACE,{"disambiguationData":[OSD([sQuery(id+"F1.wireOp",EDGE,"E2.bottom"),sQuery(id+"F1.wireOp",EDGE,"E2.top"),sQuery(id+"F1.wireOp",EDGE,"E2.left"),sQuery(id+"F1.wireOp",EDGE,"E2.right")])],"isStart":false})});
            var Q37;
            Q37=makeQuery(id+"F3.opExtrude","CAP_FACE",FACE,{"disambiguationData":[OSD([sQuery(id+"F0.wireOp",EDGE,"E0.sketch_text.stroke-717"),sQuery(id+"F0.wireOp",EDGE,"E0.sketch_text.stroke-718"),sQuery(id+"F0.wireOp",EDGE,"E0.sketch_text.stroke-719"),sQuery(id+"F0.wireOp",EDGE,"E0.sketch_text.stroke-720"),sQuery(id+"F0.wireOp",EDGE,"E0.sketch_text.stroke-721"),sQuery(id+"F0.wireOp",EDGE,"E0.sketch_text.stroke-722"),sQuery(id+"F0.wireOp",EDGE,"E0.sketch_text.stroke-723"),sQuery(id+"F0.wireOp",EDGE,"E0.sketch_text.stroke-724"),sQuery(id+"F0.wireOp",EDGE,"E0.sketch_text.stroke-725"),sQuery(id+"F0.wireOp",EDGE,"E0.sketch_text.stroke-726"),sQuery(id+"F0.wireOp",EDGE,"E0.sketch_text.stroke-727"),sQuery(id+"F0.wireOp",EDGE,"E0.sketch_text.stroke-728"),sQuery(id+"F0.wireOp",EDGE,"E0.sketch_text.stroke-729"),sQuery(id+"F0.wireOp",EDGE,"E0.sketch_text.stroke-730"),sQuery(id+"F0.wireOp",EDGE,"E0.sketch_text.stroke-731"),sQuery(id+"F0.wireOp",EDGE,"E0.sketch_text.stroke-732"),sQuery(id+"F0.wireOp",EDGE,"E0.sketch_text.stroke-733")])],"isStart":false});
            var Q38;
            Q38=makeQuery(id+"F3.opExtrude","CAP_FACE",FACE,{"disambiguationData":[OSD([sQuery(id+"F0.wireOp",EDGE,"E0.sketch_text.stroke-734"),sQuery(id+"F0.wireOp",EDGE,"E0.sketch_text.stroke-735"),sQuery(id+"F0.wireOp",EDGE,"E0.sketch_text.stroke-736"),sQuery(id+"F0.wireOp",EDGE,"E0.sketch_text.stroke-737"),sQuery(id+"F0.wireOp",EDGE,"E0.sketch_text.stroke-738"),sQuery(id+"F0.wireOp",EDGE,"E0.sketch_text.stroke-739"),sQuery(id+"F0.wireOp",EDGE,"E0.sketch_text.stroke-740"),sQuery(id+"F0.wireOp",EDGE,"E0.sketch_text.stroke-741"),sQuery(id+"F0.wireOp",EDGE,"E0.sketch_text.stroke-742"),sQuery(id+"F0.wireOp",EDGE,"E0.sketch_text.stroke-743"),sQuery(id+"F0.wireOp",EDGE,"E0.sketch_text.stroke-744"),sQuery(id+"F0.wireOp",EDGE,"E0.sketch_text.stroke-745"),sQuery(id+"F0.wireOp",EDGE,"E0.sketch_text.stroke-746"),sQuery(id+"F0.wireOp",EDGE,"E0.sketch_text.stroke-747"),sQuery(id+"F0.wireOp",EDGE,"E0.sketch_text.stroke-748"),sQuery(id+"F0.wireOp",EDGE,"E0.sketch_text.stroke-749"),sQuery(id+"F0.wireOp",EDGE,"E0.sketch_text.stroke-750"),sQuery(id+"F0.wireOp",EDGE,"E0.sketch_text.stroke-751"),sQuery(id+"F0.wireOp",EDGE,"E0.sketch_text.stroke-752"),sQuery(id+"F0.wireOp",EDGE,"E0.sketch_text.stroke-753"),sQuery(id+"F0.wireOp",EDGE,"E0.sketch_text.stroke-754"),sQuery(id+"F0.wireOp",EDGE,"E0.sketch_text.stroke-755"),sQuery(id+"F0.wireOp",EDGE,"E0.sketch_text.stroke-756"),sQuery(id+"F0.wireOp",EDGE,"E0.sketch_text.stroke-757"),sQuery(id+"F0.wireOp",EDGE,"E0.sketch_text.stroke-758")])],"isStart":false});
            var Q39;
            Q39=makeQuery(id+"F3.opExtrude","CAP_FACE",FACE,{"disambiguationData":[OSD([sQuery(id+"F0.wireOp",EDGE,"E0.sketch_text.stroke-759"),sQuery(id+"F0.wireOp",EDGE,"E0.sketch_text.stroke-760"),sQuery(id+"F0.wireOp",EDGE,"E0.sketch_text.stroke-761"),sQuery(id+"F0.wireOp",EDGE,"E0.sketch_text.stroke-762"),sQuery(id+"F0.wireOp",EDGE,"E0.sketch_text.stroke-763"),sQuery(id+"F0.wireOp",EDGE,"E0.sketch_text.stroke-764"),sQuery(id+"F0.wireOp",EDGE,"E0.sketch_text.stroke-765"),sQuery(id+"F0.wireOp",EDGE,"E0.sketch_text.stroke-766"),sQuery(id+"F0.wireOp",EDGE,"E0.sketch_text.stroke-767"),sQuery(id+"F0.wireOp",EDGE,"E0.sketch_text.stroke-768"),sQuery(id+"F0.wireOp",EDGE,"E0.sketch_text.stroke-769"),sQuery(id+"F0.wireOp",EDGE,"E0.sketch_text.stroke-770"),sQuery(id+"F0.wireOp",EDGE,"E0.sketch_text.stroke-771"),sQuery(id+"F0.wireOp",EDGE,"E0.sketch_text.stroke-772"),sQuery(id+"F0.wireOp",EDGE,"E0.sketch_text.stroke-773"),sQuery(id+"F0.wireOp",EDGE,"E0.sketch_text.stroke-774")])],"isStart":false});
            var Q40;
            Q40=makeQuery(id+"F3.opExtrude","CAP_FACE",FACE,{"disambiguationData":[OSD([sQuery(id+"F0.wireOp",EDGE,"E0.sketch_text.stroke-775"),sQuery(id+"F0.wireOp",EDGE,"E0.sketch_text.stroke-776"),sQuery(id+"F0.wireOp",EDGE,"E0.sketch_text.stroke-777"),sQuery(id+"F0.wireOp",EDGE,"E0.sketch_text.stroke-778"),sQuery(id+"F0.wireOp",EDGE,"E0.sketch_text.stroke-779"),sQuery(id+"F0.wireOp",EDGE,"E0.sketch_text.stroke-780"),sQuery(id+"F0.wireOp",EDGE,"E0.sketch_text.stroke-781"),sQuery(id+"F0.wireOp",EDGE,"E0.sketch_text.stroke-782"),sQuery(id+"F0.wireOp",EDGE,"E0.sketch_text.stroke-783"),sQuery(id+"F0.wireOp",EDGE,"E0.sketch_text.stroke-784"),sQuery(id+"F0.wireOp",EDGE,"E0.sketch_text.stroke-785"),sQuery(id+"F0.wireOp",EDGE,"E0.sketch_text.stroke-786"),sQuery(id+"F0.wireOp",EDGE,"E0.sketch_text.stroke-787"),sQuery(id+"F0.wireOp",EDGE,"E0.sketch_text.stroke-788"),sQuery(id+"F0.wireOp",EDGE,"E0.sketch_text.stroke-789")])],"isStart":false});
            var Q41;
            Q41=makeQuery(id+"F3.boolean.opBoolean","SPLIT",FACE,{"disambiguationData":[TD([makeQuery(id+"F3.opExtrude","SWEPT_FACE",FACE,{"disambiguationData":[OSD([sQuery(id+"F0.wireOp",EDGE,"E0.sketch_text.stroke-809")])]})])],"derivedFrom":makeQuery(id+"F2.opExtrude","CAP_FACE",FACE,{"disambiguationData":[OSD([sQuery(id+"F1.wireOp",EDGE,"E2.bottom"),sQuery(id+"F1.wireOp",EDGE,"E2.top"),sQuery(id+"F1.wireOp",EDGE,"E2.left"),sQuery(id+"F1.wireOp",EDGE,"E2.right")])],"isStart":false})});
            var Q42;
            Q42=makeQuery(id+"F3.opExtrude","CAP_FACE",FACE,{"disambiguationData":[OSD([sQuery(id+"F0.wireOp",EDGE,"E0.sketch_text.stroke-817"),sQuery(id+"F0.wireOp",EDGE,"E0.sketch_text.stroke-818"),sQuery(id+"F0.wireOp",EDGE,"E0.sketch_text.stroke-819"),sQuery(id+"F0.wireOp",EDGE,"E0.sketch_text.stroke-820"),sQuery(id+"F0.wireOp",EDGE,"E0.sketch_text.stroke-821"),sQuery(id+"F0.wireOp",EDGE,"E0.sketch_text.stroke-822"),sQuery(id+"F0.wireOp",EDGE,"E0.sketch_text.stroke-823"),sQuery(id+"F0.wireOp",EDGE,"E0.sketch_text.stroke-824"),sQuery(id+"F0.wireOp",EDGE,"E0.sketch_text.stroke-825"),sQuery(id+"F0.wireOp",EDGE,"E0.sketch_text.stroke-826"),sQuery(id+"F0.wireOp",EDGE,"E0.sketch_text.stroke-827"),sQuery(id+"F0.wireOp",EDGE,"E0.sketch_text.stroke-828"),sQuery(id+"F0.wireOp",EDGE,"E0.sketch_text.stroke-829")])],"isStart":false});
            var Q43;
            Q43=makeQuery(id+"F3.boolean.opBoolean","SPLIT",FACE,{"disambiguationData":[TD([makeQuery(id+"F3.opExtrude","SWEPT_FACE",FACE,{"disambiguationData":[OSD([sQuery(id+"F0.wireOp",EDGE,"E0.sketch_text.stroke-845")])]})])],"derivedFrom":makeQuery(id+"F2.opExtrude","CAP_FACE",FACE,{"disambiguationData":[OSD([sQuery(id+"F1.wireOp",EDGE,"E2.bottom"),sQuery(id+"F1.wireOp",EDGE,"E2.top"),sQuery(id+"F1.wireOp",EDGE,"E2.left"),sQuery(id+"F1.wireOp",EDGE,"E2.right")])],"isStart":false})});
            var Q44;
            Q44=makeQuery(id+"F3.opExtrude","CAP_FACE",FACE,{"disambiguationData":[OSD([sQuery(id+"F0.wireOp",EDGE,"E0.sketch_text.stroke-854"),sQuery(id+"F0.wireOp",EDGE,"E0.sketch_text.stroke-855"),sQuery(id+"F0.wireOp",EDGE,"E0.sketch_text.stroke-856"),sQuery(id+"F0.wireOp",EDGE,"E0.sketch_text.stroke-857")])],"isStart":false});
            var Q45;
            Q45=makeQuery(id+"F3.opExtrude","CAP_FACE",FACE,{"disambiguationData":[OSD([sQuery(id+"F0.wireOp",EDGE,"E0.sketch_text.stroke-858"),sQuery(id+"F0.wireOp",EDGE,"E0.sketch_text.stroke-859"),sQuery(id+"F0.wireOp",EDGE,"E0.sketch_text.stroke-860"),sQuery(id+"F0.wireOp",EDGE,"E0.sketch_text.stroke-861"),sQuery(id+"F0.wireOp",EDGE,"E0.sketch_text.stroke-862"),sQuery(id+"F0.wireOp",EDGE,"E0.sketch_text.stroke-863"),sQuery(id+"F0.wireOp",EDGE,"E0.sketch_text.stroke-864")])],"isStart":false});
            var Q46;
            Q46=makeQuery(id+"F3.boolean.opBoolean","SPLIT",FACE,{"disambiguationData":[TD([makeQuery(id+"F3.opExtrude","SWEPT_FACE",FACE,{"disambiguationData":[OSD([sQuery(id+"F0.wireOp",EDGE,"E0.sketch_text.stroke-258")])]})])],"derivedFrom":makeQuery(id+"F2.opExtrude","CAP_FACE",FACE,{"disambiguationData":[OSD([sQuery(id+"F1.wireOp",EDGE,"E2.bottom"),sQuery(id+"F1.wireOp",EDGE,"E2.top"),sQuery(id+"F1.wireOp",EDGE,"E2.left"),sQuery(id+"F1.wireOp",EDGE,"E2.right")])],"isStart":false})});
            extrude(context, id + "F4", {"entities" : qUnion([Q0, Q1, Q2, Q3, Q4, Q5, Q6, Q7, Q8, Q9, Q10, Q11, Q12, Q13, Q14, Q15, Q16, Q17, Q18, Q19, Q20, Q21, Q22, Q23, Q24, Q25, Q26, Q27, Q28, Q29, Q30, Q31, Q32, Q33, Q34, Q35, Q36, Q37, Q38, Q39, Q40, Q41, Q42, Q43, Q44, Q45, Q46]), "operationType" : NewBodyOperationType.REMOVE, "endBound" : BoundingType.THROUGH_ALL, "oppositeDirection" : true, "depth" : 25 * mm, "hasSecondDirection" : true, "secondDirectionBound" : SecondDirectionBoundingType.THROUGH_ALL, "secondDirectionOppositeDirection" : false, "secondDirectionDepth" : 25 * mm});
        }
        {
            var Q0;
            Q0=makeQuery(id+"F2.opExtrude","SWEPT_EDGE",EDGE,{"disambiguationData":[OSD([sQuery(id+"F1.wireOp",EDGE,"E2.top"),sQuery(id+"F1.wireOp",EDGE,"E2.left")])]});
            var Q1;
            Q1=makeQuery(id+"F2.opExtrude","SWEPT_EDGE",EDGE,{"disambiguationData":[OSD([sQuery(id+"F1.wireOp",EDGE,"E2.top"),sQuery(id+"F1.wireOp",EDGE,"E2.right")])]});
            var Q2;
            Q2=makeQuery(id+"F2.opExtrude","SWEPT_EDGE",EDGE,{"disambiguationData":[OSD([sQuery(id+"F1.wireOp",EDGE,"E2.bottom"),sQuery(id+"F1.wireOp",EDGE,"E2.right")])]});
            var Q3;
            Q3=makeQuery(id+"F2.opExtrude","SWEPT_EDGE",EDGE,{"disambiguationData":[OSD([sQuery(id+"F1.wireOp",EDGE,"E2.bottom"),sQuery(id+"F1.wireOp",EDGE,"E2.left")])]});
            fillet(context, id + "F5", {"entities" : qUnion([Q0, Q1, Q2, Q3]), "radius" : 10 * mm, "tangentPropagation" : true, "allowEdgeOverflow" : false});
        }
    });
